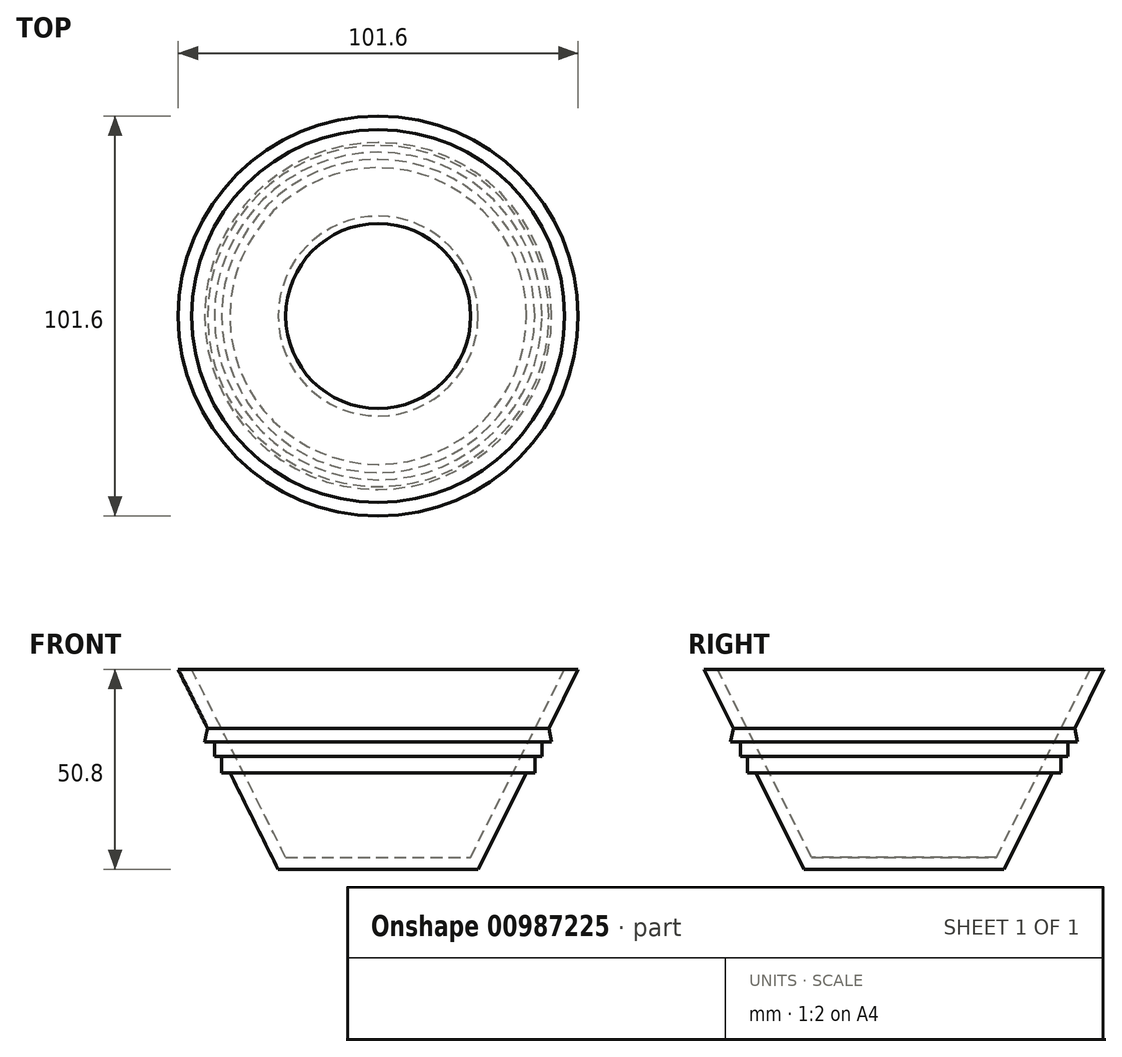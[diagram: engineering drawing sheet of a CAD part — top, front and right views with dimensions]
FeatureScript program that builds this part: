
annotation { "Feature Type Name" : "Feature", "Feature Type Description" : "" }
export const myFeature = defineFeature(function(context is Context, id is Id, definition is map)
    precondition{}
    {
        {
            var Q0;
            Q0=qCreatedBy(makeId("Front.planeOp"),FACE);
            var sketch = newSketch(context, id + "F0", { "sketchPlane" : qUnion([Q0])});
            skLineSegment(sketch, "E0", {"start": v(0, 0) * mm, "end": v(0, 50.8) * mm, "construction": true});
            skLineSegment(sketch, "E1", {"start": v(0, 0) * mm, "end": v(25.4, 0) * mm});
            skLineSegment(sketch, "E2", {"start": v(25.4, 0) * mm, "end": v(50.8, 50.8) * mm});
            skLineSegment(sketch, "E3.0", {"start": v(23.5, 3.07) * mm, "end": v(47.36, 50.8) * mm});
            skLineSegment(sketch, "E3.1", {"start": v(0, 3.07) * mm, "end": v(23.5, 3.07) * mm});
            skLineSegment(sketch, "E4", {"start": v(0, 3.07) * mm, "end": v(0, 0) * mm});
            skLineSegment(sketch, "E5", {"start": v(47.36, 50.8) * mm, "end": v(50.8, 50.8) * mm});
            skLineSegment(sketch, "E6", {"start": v(43.34, 35.88) * mm, "end": v(44.09, 32.4) * mm});
            skLineSegment(sketch, "E7", {"start": v(44.09, 32.4) * mm, "end": v(41.6, 32.4) * mm});
            skLineSegment(sketch, "E8", {"start": v(41.6, 32.4) * mm, "end": v(41.6, 28.77) * mm});
            skLineSegment(sketch, "E9", {"start": v(41.6, 28.77) * mm, "end": v(39.79, 28.77) * mm});
            skLineSegment(sketch, "E10", {"start": v(39.79, 28.77) * mm, "end": v(39.79, 24.57) * mm});
            skLineSegment(sketch, "E11", {"start": v(39.79, 24.57) * mm, "end": v(37.68, 24.57) * mm});
            skSolve(sketch);
        }
        {
            var Q0;
            Q0=makeQuery(id+"F0.imprint","IMPRINT",FACE,{"disambiguationData":[TD([[makeQuery(id+"F0.imprint","IMPRINT",EDGE,{"derivedFrom":sQuery(id+"F0.wireOp",EDGE,"E1")}),1.0]])]});
            var Q1;
            {var subQ0=sQuery(id+"F0.wireOp",EDGE,"E6");Q1=makeQuery(id+"F0.imprint","IMPRINT",FACE,{"disambiguationData":[TD([[makeQuery(id+"F0.imprint","IMPRINT",EDGE,{"derivedFrom":subQ0}),-1.0]])]});}
            var Q2;
            {var subQ0=sQuery(id+"F0.wireOp",EDGE,"E8");Q2=makeQuery(id+"F0.imprint","IMPRINT",FACE,{"disambiguationData":[TD([[makeQuery(id+"F0.imprint","IMPRINT",EDGE,{"derivedFrom":subQ0}),-1.0]])]});}
            var Q3;
            {var subQ0=sQuery(id+"F0.wireOp",EDGE,"E10");Q3=makeQuery(id+"F0.imprint","IMPRINT",FACE,{"disambiguationData":[TD([[makeQuery(id+"F0.imprint","IMPRINT",EDGE,{"derivedFrom":subQ0}),-1.0]])]});}
            var Q4;
            Q4=sQuery(id+"F0.wireOp",EDGE,"E0");
            revolve(context, id + "F1", {"surfaceOperationType" : NewSurfaceOperationType.NEW, "entities" : qUnion([Q0, Q1, Q2, Q3]), "axis" : qUnion([Q4]), "revolveType" : RevolveType.FULL});
        }
    });
